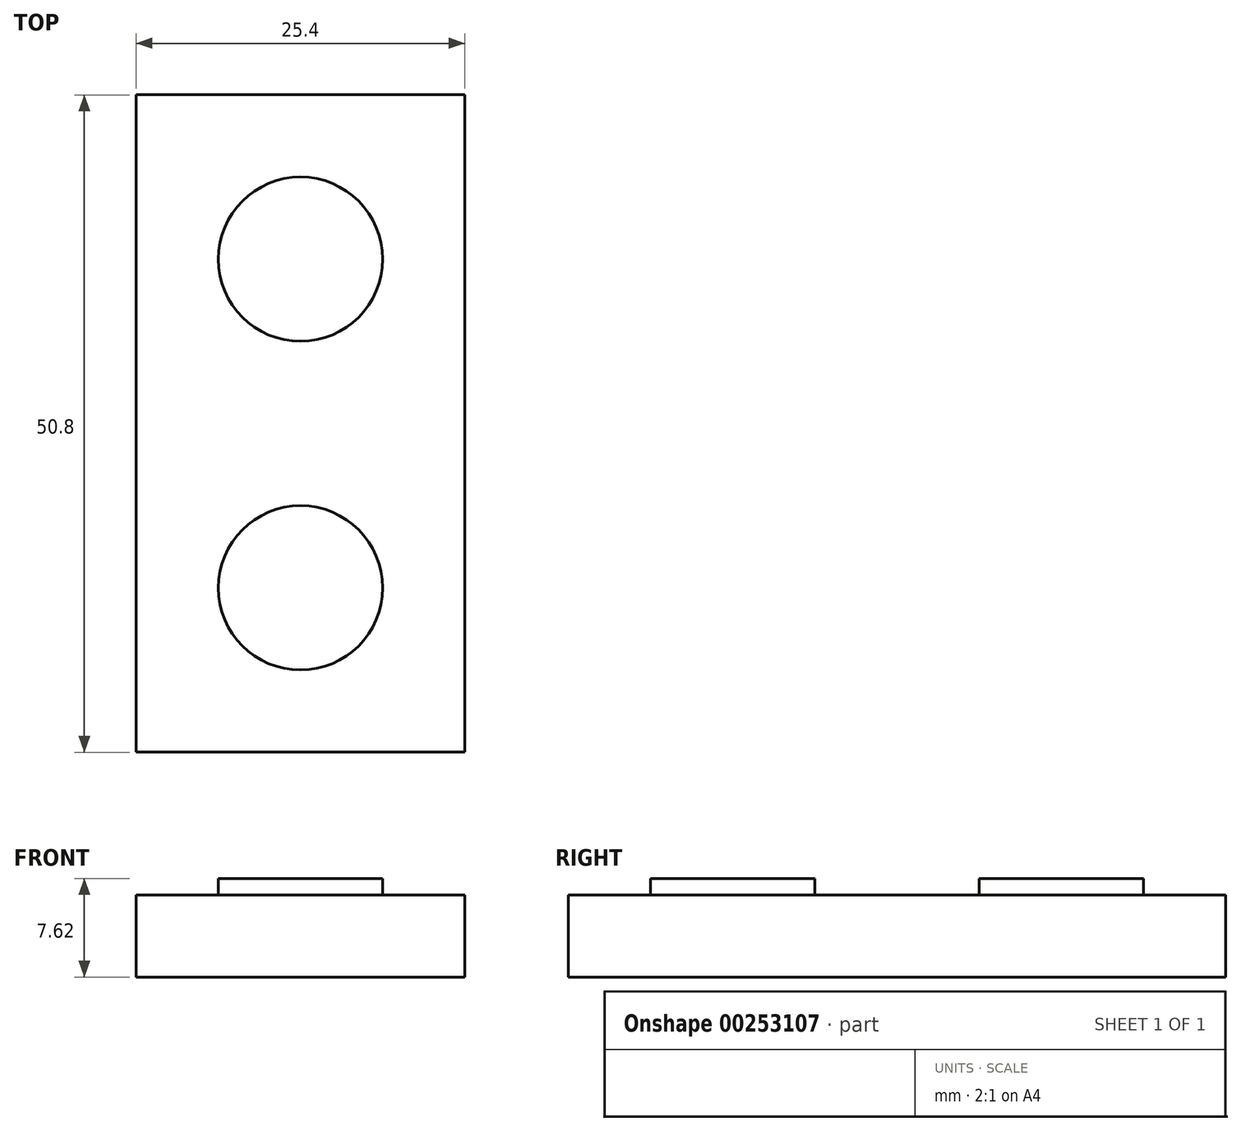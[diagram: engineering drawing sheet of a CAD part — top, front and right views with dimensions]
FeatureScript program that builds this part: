
annotation { "Feature Type Name" : "Feature", "Feature Type Description" : "" }
export const myFeature = defineFeature(function(context is Context, id is Id, definition is map)
    precondition{}
    {
        {
            var Q0;
            Q0=qCreatedBy(makeId("Top.planeOp"),FACE);
            var sketch = newSketch(context, id + "F0", { "sketchPlane" : qUnion([Q0])});
            skLineSegment(sketch, "E0.bottom", {"start": v(-6.62, 23.64) * mm, "end": v(18.78, 23.64) * mm});
            skLineSegment(sketch, "E0.top", {"start": v(-6.62, -27.16) * mm, "end": v(18.78, -27.16) * mm});
            skLineSegment(sketch, "E0.left", {"start": v(-6.62, 23.64) * mm, "end": v(-6.62, -27.16) * mm});
            skLineSegment(sketch, "E0.right", {"start": v(18.78, 23.64) * mm, "end": v(18.78, -27.16) * mm});
            skLineSegment(sketch, "E1", {"start": v(-6.62, 23.64) * mm, "end": v(-6.62, 10.94) * mm});
            skLineSegment(sketch, "E2", {"start": v(-6.62, -27.16) * mm, "end": v(-6.62, -14.46) * mm});
            skCircle(sketch, "E3", {"center": v(6.08, 10.94) * mm, "radius": 6.35 * mm});
            skPoint(sketch, "E3.centerSnap0", {"position": v(6.08, 23.64) * mm});
            skCircle(sketch, "E4", {"center": v(6.08, -14.46) * mm, "radius": 6.35 * mm});
            skSolve(sketch);
        }
        {
            var Q0;
            Q0 = qSketchRegion(id + "F0", true);
            extrude(context, id + "F1", {"entities" : qUnion([Q0]), "depth" : 6.35 * mm});
        }
        {
            var Q0;
            Q0=makeQuery(id+"F0.imprint","IMPRINT",FACE,{"disambiguationData":[TD([[makeQuery(id+"F0.imprint","IMPRINT",EDGE,{"derivedFrom":sQuery(id+"F0.wireOp",EDGE,"E3")}),1.0]])]});
            var Q1;
            Q1=makeQuery(id+"F0.imprint","IMPRINT",FACE,{"disambiguationData":[TD([[makeQuery(id+"F0.imprint","IMPRINT",EDGE,{"derivedFrom":sQuery(id+"F0.wireOp",EDGE,"E4")}),1.0]])]});
            extrude(context, id + "F2", {"entities" : qUnion([Q0, Q1]), "operationType" : NewBodyOperationType.ADD, "depth" : 7.62 * mm});
        }
    });
